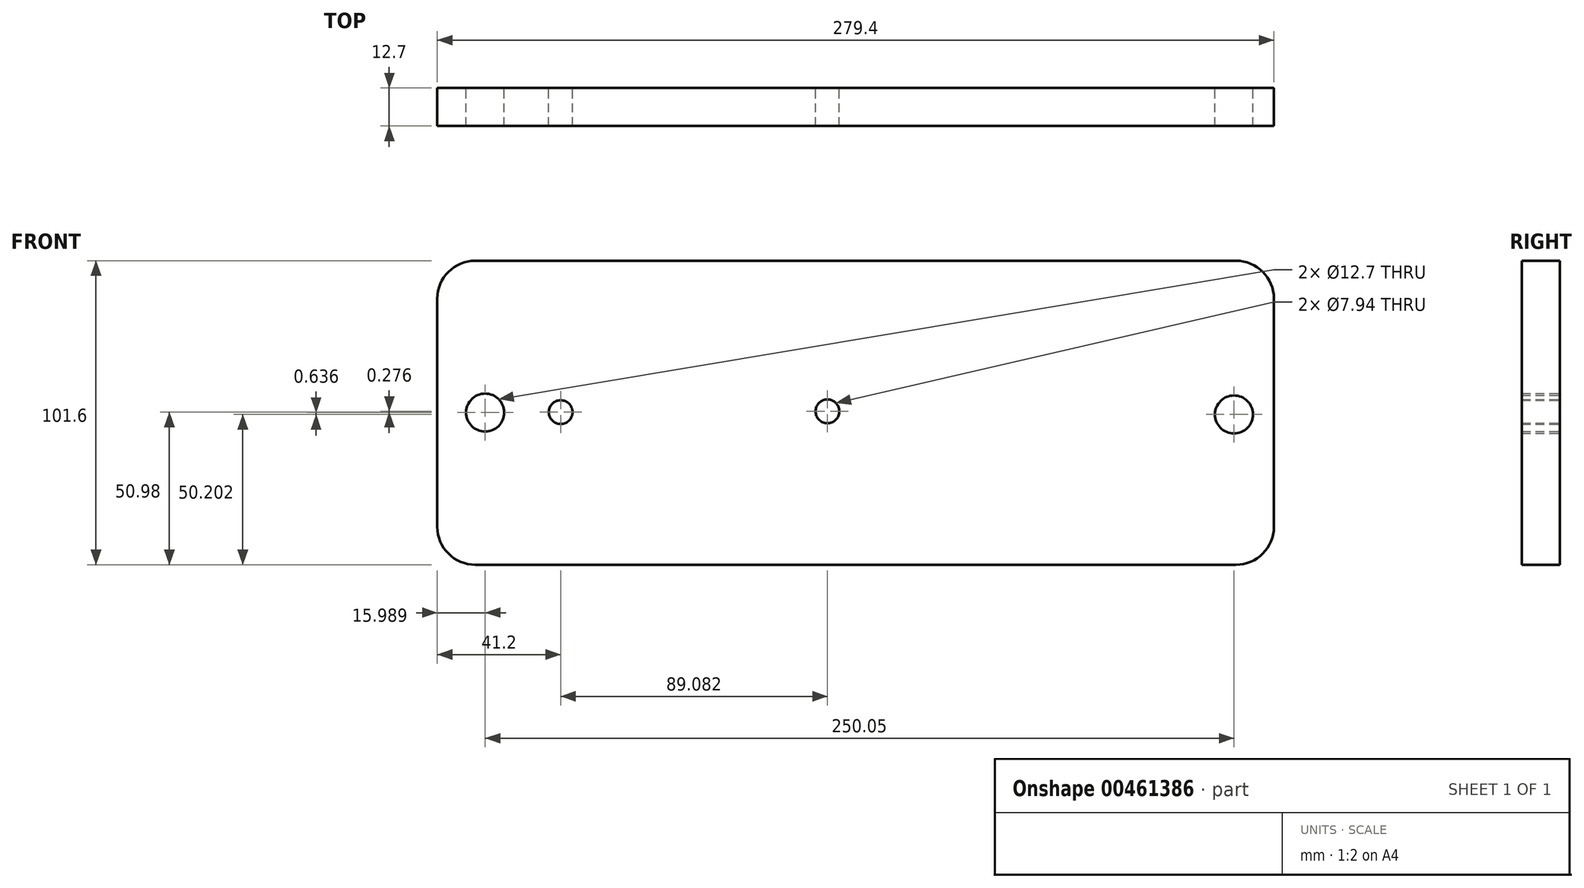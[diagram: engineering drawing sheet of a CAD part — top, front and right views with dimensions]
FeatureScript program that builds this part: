
annotation { "Feature Type Name" : "Feature", "Feature Type Description" : "" }
export const myFeature = defineFeature(function(context is Context, id is Id, definition is map)
    precondition{}
    {
        {
            var Q0;
            Q0=qCreatedBy(makeId("Front.planeOp"),FACE);
            var sketch = newSketch(context, id + "F0", { "sketchPlane" : qUnion([Q0])});
            skLineSegment(sketch, "E0.bottom", {"start": v(0, 0) * mm, "end": v(279.4, 0) * mm});
            skLineSegment(sketch, "E0.top", {"start": v(0, 101.6) * mm, "end": v(279.4, 101.6) * mm});
            skLineSegment(sketch, "E0.left", {"start": v(0, 0) * mm, "end": v(0, 101.6) * mm});
            skLineSegment(sketch, "E0.right", {"start": v(279.4, 0) * mm, "end": v(279.4, 101.6) * mm});
            skSolve(sketch);
        }
        {
            var Q0;
            Q0 = qSketchRegion(id + "F0", true);
            extrude(context, id + "F1", {"entities" : qUnion([Q0]), "depth" : 12.7 * mm});
        }
        {
            var Q0;
            Q0=makeQuery(id+"F1.opExtrude","SWEPT_EDGE",EDGE,{"disambiguationData":[OSD([sQuery(id+"F0.wireOp",EDGE,"E0.top"),sQuery(id+"F0.wireOp",EDGE,"E0.left")])]});
            var Q1;
            Q1=makeQuery(id+"F1.opExtrude","SWEPT_EDGE",EDGE,{"disambiguationData":[OSD([sQuery(id+"F0.wireOp",EDGE,"E0.top"),sQuery(id+"F0.wireOp",EDGE,"E0.right")])]});
            var Q2;
            Q2=makeQuery(id+"F1.opExtrude","SWEPT_EDGE",EDGE,{"disambiguationData":[OSD([sQuery(id+"F0.wireOp",EDGE,"E0.bottom"),sQuery(id+"F0.wireOp",EDGE,"E0.right")])]});
            var Q3;
            Q3=makeQuery(id+"F1.opExtrude","SWEPT_EDGE",EDGE,{"disambiguationData":[OSD([sQuery(id+"F0.wireOp",EDGE,"E0.bottom"),sQuery(id+"F0.wireOp",EDGE,"E0.left")])]});
            fillet(context, id + "F2", {"entities" : qUnion([Q0, Q1, Q2, Q3]), "radius" : 12.7 * mm, "tangentPropagation" : true, "allowEdgeOverflow" : false});
        }
        {
            var Q0;
            Q0=qCreatedBy(makeId("Front.planeOp"),FACE);
            var sketch = newSketch(context, id + "F3", { "sketchPlane" : qUnion([Q0])});
            skCircle(sketch, "E1", {"center": v(15.99, 50.84) * mm, "radius": 6.35 * mm});
            skCircle(sketch, "E2", {"center": v(41.2, 50.98) * mm, "radius": 3.97 * mm});
            skCircle(sketch, "E3", {"center": v(130.28, 51.26) * mm, "radius": 3.97 * mm});
            skCircle(sketch, "E4", {"center": v(266.04, 50.2) * mm, "radius": 6.35 * mm});
            skSolve(sketch);
        }
        {
            var Q0;
            Q0 = qSketchRegion(id + "F3", true);
            var Q1;
            Q1=sQuery(id+"F3.wireOp",EDGE,"E1");
            var Q2;
            Q2=sQuery(id+"F3.wireOp",EDGE,"E2");
            var Q3;
            Q3=sQuery(id+"F3.wireOp",EDGE,"E3");
            var Q4;
            Q4=sQuery(id+"F3.wireOp",EDGE,"E4");
            extrude(context, id + "F4", {"entities" : qUnion([Q0]), "operationType" : NewBodyOperationType.REMOVE, "surfaceEntities" : qUnion([Q1, Q2, Q3, Q4]), "oppositeDirection" : true, "depth" : -22.86 * mm});
        }
    });
